# Revit family: LCAD
name_source: partatom
category: Lighting Fixtures
units: mm (PartAtom-declared; Revit-internal decimal feet)

## family parameters
Always vertical = Yes
Cut with Voids When Loaded = No
Host = Wall
Light Source = Yes
OmniClass Number = 23.80.70.11.14
OmniClass Title = General Luminaries, Directional
Part Type = Normal
Room Calculation Point = No
Round Connector Dimension = Use Diameter
Shared = No

## types (3) — shared parameters
Assembly Code = D5020200
Color Filter = 16777215
Description = LED Cadillac
Dimming Lamp Color Temperature Shift = <None>
Housing Finish = Metal - Viscor - White
Lamp = LED
Lens Finish = Acrylic - Viscor - Frosted Prismatic P12
Manufacturer = VISIONEERING by VISCOR
Model = LCAD
Tilt Angle = 180.00°
URL = https://www.viscor.com
Voltage = 120 V

## per-type parameters (varying)
| type | Apparent Load | Emit from Line Length | Lamp Wattage | Length | Photometric Web File |
| LCAD24-LED840K020LUNV-P12 | 17 VA | 2' - 0" | 17 VA | 2' - 0" | LCAD24-LED840K020LUNV-P12.ies |
| LCAD48-LED840K037LUNV-P12 | 28 VA | 4' - 0" | 28 VA | 4' - 0" | LCAD48-LED840K037LUNV-P12.ies |
| LCAD96-LED840K074LUNV-P12 | 54 VA | 8' - 0" | 54 VA | 8' - 0" | LCAD96-LED840K074LUNV-P12.ies |

## geometry (parser evidence)
native form markers: Sweep x2
no freeform markers — native parametric forms only
